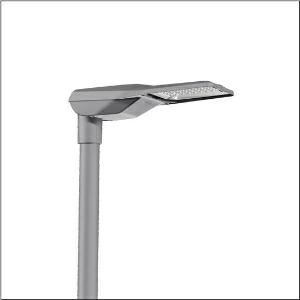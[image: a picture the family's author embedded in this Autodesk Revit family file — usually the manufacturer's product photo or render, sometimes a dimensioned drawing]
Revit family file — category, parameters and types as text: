
# Revit family: streetlight_sl_21_iq_mini___st1_0a_5xe2d21g08hb_8dd2
name_source: partatom
category: Lighting Fixtures
units: mm (PartAtom-declared; Revit-internal decimal feet)

## family parameters
Cut with Voids When Loaded = No
Host = Face
Light Source = No
Part Type = Normal
Room Calculation Point = No
Round Connector Dimension = Use Diameter
Shared = No

## types (1)
- --- (1 x LED, 7830 lm, 70.9 W, 2200K)
    Apparent Load = 71 VA
    CIE Flux Codes = 37 72 97 100 100
    Color Rendering = 70
    Color Temperature = 2200K
    Default Elevation = 1800 mm
    Description = Streetlight SL 21 iQ mini, mast luminaire, primary light control with lens, of PMMA, primary optical cover: cover, of toughened safety glass, transparent, light distribution: ST1.0a, light emission: direct distribution, primary light characteristic: asymmetric, installation type: post-top, side-entry, LED, High Power LED, rated luminous flux: 7.830lm, luminous efficacy: 110lm/W, light colour: 722, colour temperature: 2200K, control: Street-Remote, Auto-Match, Temp-Guard, Lumen-Switch, Night-Set, Smart-Wire, Light-Fading, Desk-Remote (wireless, voltage-free reading and setting of iQ features in the workshop via application-optimized NFC function/RFID function), optimised constant luminous flux control (CLO 2.0), presetting dimming linear, mains connection: 220..240V, AC, 50/60Hz, start of lifetime: 71W, end of service life: 75W, reduction: 31W, luminaire housing, of diecast aluminium, powder-coated, Siteco® metallic grey (DB 702S), corrosivity category C5 mid according to DIN EN ISO 12944, please order mast flange separately, inclination adjustable: 0°, 5°, 10°, 15°, sealing non-destructively replaceable, multi-level sealing system, length: 628mm, width: 235mm, height: 110mm, mast flange for spigot size: 42mm (side-entry): 5XC10008XM4, 60/48mm (side-entry/post-top): 5XC10108XM2, 76/60mm (side-entry/post-top): 5XC10108XM1, protection rating (complete): IP66, insulation class (complete): insulation class II (safety insulation), certification: CE, ENEC, ENEC+, VDE, impact resistance: IK09, permissible operating ambient temperature for outdoor applications: -40..+50°C, standard-compliant lighting for roads and squares, packaging unit: 1 piece

Light Distribution: ST1.0a
    Height = 110 mm
    Lamp = 1 x LED
    Lamp Light Flux = 7830 lm
    Lamp Power = 70.9 W
    Lamp count = 1
    Length = 625 mm
    Luminous efficacy = 110 lm/W
    Manufacturer = Siteco
    ModVariant = No
    Model = 5XE2D21G08HB
    Number of Poles = 1
    OnlyDefault = Yes
    Power Factor = 1
    Product Name = Streetlight SL 21 iQ mini | ST1.0a
    Product group = mast luminaire | pylon top
    ProductGroupID = 6100
    Protection Class = Protection class II
    Protection Degree = IP 66
    RLX_Detail_Level = 1
    RLX_Emergency_Light_Flux = 0 lm
    RLX_Emergency_Type = 0
    RLX_Emergency_Type_DB = No
    RlxData = <blob elided: 93133 chars, md5=a07a87e8>
    Socket = socket
    Standby Power = 0 W
    System Light Flux = 7830 lm
    System Power = 71 W
    Type Comments = factory setting: luminous flux: 100 % | dim-lin: 254 | 711 mA
    Type Image = l_1003519.jpg
    URL = http://relux.com
    VarID = @adj_090609
    Voltage = 0 V
    Weight = 0.00 kg
    Width = 234 mm

## geometry (parser evidence)
native form markers: Blend x4, Sweep x13
no freeform markers — native parametric forms only
